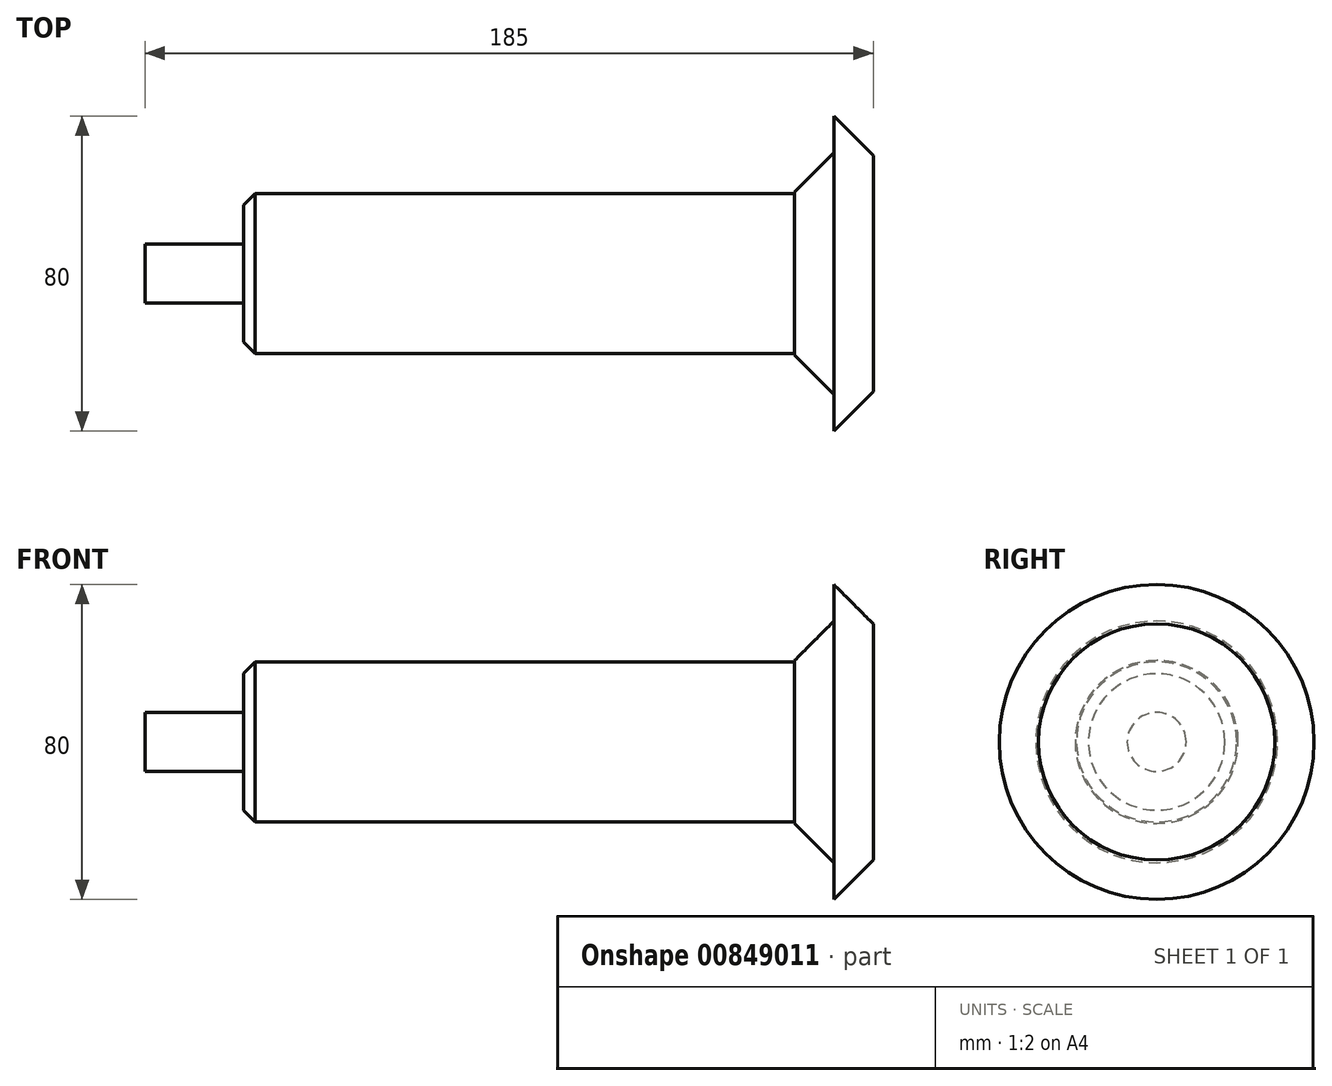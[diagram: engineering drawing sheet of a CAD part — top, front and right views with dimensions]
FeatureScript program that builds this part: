
annotation { "Feature Type Name" : "Feature", "Feature Type Description" : "" }
export const myFeature = defineFeature(function(context is Context, id is Id, definition is map)
    precondition{}
    {
        {
            var Q0;
            Q0=qCreatedBy(makeId("Top.planeOp"),FACE);
            var sketch = newSketch(context, id + "F0", { "sketchPlane" : qUnion([Q0])});
            skLineSegment(sketch, "E0.bottom", {"start": v(0, 0) * mm, "end": v(-25, 0) * mm});
            skLineSegment(sketch, "E0.top", {"start": v(0, 7.5) * mm, "end": v(-25, 7.5) * mm});
            skLineSegment(sketch, "E0.left", {"start": v(0, 0) * mm, "end": v(0, 7.5) * mm});
            skLineSegment(sketch, "E0.right", {"start": v(-25, 0) * mm, "end": v(-25, 7.5) * mm});
            skLineSegment(sketch, "E1.bottom", {"start": v(0, 0) * mm, "end": v(140, 0) * mm});
            skLineSegment(sketch, "E1.top", {"start": v(0, 20.35) * mm, "end": v(140, 20.35) * mm});
            skLineSegment(sketch, "E1.left", {"start": v(0, 0) * mm, "end": v(0, 20.35) * mm});
            skLineSegment(sketch, "E1.right", {"start": v(140, 0) * mm, "end": v(140, 20.35) * mm});
            skLineSegment(sketch, "E2.bottom", {"start": v(140, 0) * mm, "end": v(150, 0) * mm});
            skLineSegment(sketch, "E2.top", {"start": v(140, 30.7) * mm, "end": v(150, 30.7) * mm});
            skLineSegment(sketch, "E2.left", {"start": v(140, 0) * mm, "end": v(140, 30.7) * mm});
            skLineSegment(sketch, "E2.right", {"start": v(150, 0) * mm, "end": v(150, 30.7) * mm});
            skLineSegment(sketch, "E3.bottom", {"start": v(150, 0) * mm, "end": v(160, 0) * mm});
            skLineSegment(sketch, "E3.top", {"start": v(150, 40) * mm, "end": v(160, 40) * mm});
            skLineSegment(sketch, "E3.left", {"start": v(150, 0) * mm, "end": v(150, 40) * mm});
            skLineSegment(sketch, "E3.right", {"start": v(160, 0) * mm, "end": v(160, 40) * mm});
            skSolve(sketch);
        }
        {
            var Q0;
            {var subQ0=sQuery(id+"F0.wireOp",EDGE,"E0.bottom");Q0=makeQuery(id+"F0.imprint","IMPRINT",FACE,{"disambiguationData":[TD([[makeQuery(id+"F0.imprint","IMPRINT",EDGE,{"derivedFrom":subQ0}),-1.0]])]});}
            var Q1;
            {var subQ3=sQuery(id+"F0.wireOp",EDGE,"E1.bottom");Q1=makeQuery(id+"F0.imprint","IMPRINT",FACE,{"disambiguationData":[TD([[makeQuery(id+"F0.imprint","IMPRINT",EDGE,{"derivedFrom":subQ3}),1.0]])]});}
            var Q2;
            {var subQ3=sQuery(id+"F0.wireOp",EDGE,"E2.bottom");Q2=makeQuery(id+"F0.imprint","IMPRINT",FACE,{"disambiguationData":[TD([[makeQuery(id+"F0.imprint","IMPRINT",EDGE,{"derivedFrom":subQ3}),1.0]])]});}
            var Q3;
            {var subQ3=sQuery(id+"F0.wireOp",EDGE,"E3.bottom");Q3=makeQuery(id+"F0.imprint","IMPRINT",FACE,{"disambiguationData":[TD([[makeQuery(id+"F0.imprint","IMPRINT",EDGE,{"derivedFrom":subQ3}),1.0]])]});}
            var Q4;
            Q4=sQuery(id+"F0.wireOp",EDGE,"E1.bottom");
            revolve(context, id + "F1", {"surfaceOperationType" : NewSurfaceOperationType.NEW, "entities" : qUnion([Q0, Q1, Q2, Q3]), "axis" : qUnion([Q4]), "revolveType" : RevolveType.FULL});
        }
        {
            var Q0;
            Q0=makeQuery(id+"F1.opRevolve","SWEPT_EDGE",EDGE,{"disambiguationData":[OSD([sQuery(id+"F0.wireOp",EDGE,"E1.top"),sQuery(id+"F0.wireOp",EDGE,"E1.left")])]});
            chamfer(context, id + "F2", {"entities" : qUnion([Q0]), "chamferType" : ChamferType.OFFSET_ANGLE, "width" : 3 * mm, "oppositeDirection" : false, "angle" : 45 * degree, "tangentPropagation" : true});
        }
        {
            var Q0;
            Q0=makeQuery(id+"F1.opRevolve","SWEPT_EDGE",EDGE,{"disambiguationData":[OSD([sQuery(id+"F0.wireOp",EDGE,"E2.top"),sQuery(id+"F0.wireOp",EDGE,"E2.left")])]});
            chamfer(context, id + "F3", {"entities" : qUnion([Q0]), "chamferType" : ChamferType.OFFSET_ANGLE, "width" : 10 * mm, "oppositeDirection" : false, "angle" : 45 * degree, "tangentPropagation" : true});
        }
        {
            var Q0;
            Q0=makeQuery(id+"F1.opRevolve","SWEPT_EDGE",EDGE,{"disambiguationData":[OSD([sQuery(id+"F0.wireOp",EDGE,"E3.top"),sQuery(id+"F0.wireOp",EDGE,"E3.right")])]});
            chamfer(context, id + "F4", {"entities" : qUnion([Q0]), "chamferType" : ChamferType.OFFSET_ANGLE, "width" : 10 * mm, "oppositeDirection" : true, "angle" : 45 * degree, "tangentPropagation" : true});
        }
    });
